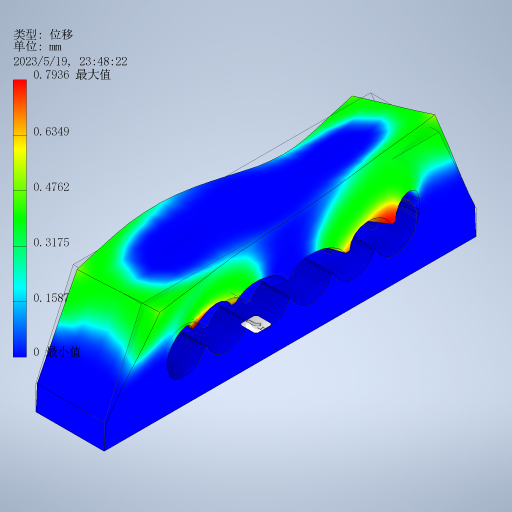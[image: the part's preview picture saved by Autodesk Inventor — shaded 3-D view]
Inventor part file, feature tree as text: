
AUTODESK INVENTOR PART (.ipt)
format: ipt  version: 2023 (Build 270158000, 158)  size: 535,552 bytes
history: native  units: mm
features: sketch x13, extrude x7, plane x6, loft x1
ambient origin geometry x8: Origin, YZ Plane, XZ Plane, XY Plane, X Axis, Y Axis, Z Axis, Center Point
bodies: 实体1 (feature_tree)
feature tree (27):
  extrude  "拉伸1"  Depth=20.0mm
  sketch  "草图2"  dims[d3=1.0mm d4=0.0mm d5=-1.5mm]
  plane  "工作平面1"
  extrude  "拉伸2"  [1 undecoded]
  extrude  "拉伸3"  Depth=12.0mm
  plane  "工作平面3"
  sketch  "草图6"  dims[d13=12.0mm d14=0.0mm d39=0.85mm]
  extrude  "拉伸5"  Depth=12.0mm TaperAngle=0.0deg
  sketch  "草图8"  dims[d44=-5.0mm d54=1.7mm]
  plane  "工作平面4"
  plane  "工作平面5"
  sketch  "草图10"  dims[d56=60.0mm d58=1.7mm d59=10.0mm d61=10.0mm d63=7.5mm]
  plane  "工作平面6"
  loft  "放样1"
  extrude  "拉伸6"  TaperAngle=0.0deg  [1 undecoded]
  extrude  "拉伸7"  Depth=1.7mm
  sketch  "草图14"  dims[d74=2.4mm]
  extrude  "拉伸8"  Depth=10.0mm
  sketch  "草图1"  dims[d1=15.0mm d2=20.0mm]
  sketch  "草图3"  dims[d6=3.4mm d8=12.0mm]
  sketch  "草图4"  dims[d10=0.0mm d11=12.0mm d12=0.0mm]
  plane  "工作平面2"
  sketch  "草图7"  dims[d41=45.0deg d42=0.0mm d43=0.0mm]
  sketch  "草图11"  dims[d64=1.7mm]
  sketch  "草图12"  dims[d66=60.0mm d68=1.7mm d69=10.0mm d71=10.0mm]
  sketch  "草图13"  dims[d73=7.5mm]
  sketch  "草图15"  dims[d75=1.8mm d76=7.0mm d77=0.0mm d78=90.0deg d79=0.0mm d80=90.0deg d81=0.0mm d82=90.0deg d83=0.0mm d84=90.0deg d85=60.0mm d87=1.7mm d88=10.0mm d90=10.0mm d92=0.0mm d93=0.0mm d94=0.1mm d95=0.7mm d96=0.7mm d97=0.7mm d98=10.0mm d99=0.0mm d100=1.2mm d101=1.2mm d102=17.25mm d103=0.0mm]
note: 2 required parameter values undecoded (feature->parameter linkage not recoverable at this tier; creation-order binding heuristic only, values carry confidence <= 0.55)
